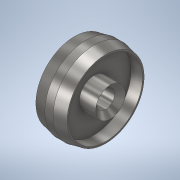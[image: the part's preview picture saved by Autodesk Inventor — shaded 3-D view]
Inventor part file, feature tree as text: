
AUTODESK INVENTOR PART (.ipt)
format: ipt  version: 2020 (Build 240168000, 168)  size: 775,168 bytes
history: native  units: mm
features: revolve x1, sketch x1
ambient origin geometry x8: Origin, YZ Plane, XZ Plane, XY Plane, X Axis, Y Axis, Z Axis, Center Point
bodies: Solid1 (feature_tree)
feature tree (2):
  revolve  "Revolution1"  [1 undecoded]
  sketch  "Sketch1"  dims[d0=50.0mm d1=18.0mm d2=38.0mm d3=11.0mm d4=39.0mm d5=27.0mm d8=10.0mm d9=20.0mm d10=90.0deg d11=34.0mm d12=2.0mm d13=2.0mm d14=18.0mm d15=26.248585mm d16=11.714245mm d17=18.0mm d18=45.0mm]
note: 1 required parameter value undecoded (feature->parameter linkage not recoverable at this tier; creation-order binding heuristic only, values carry confidence <= 0.55)
